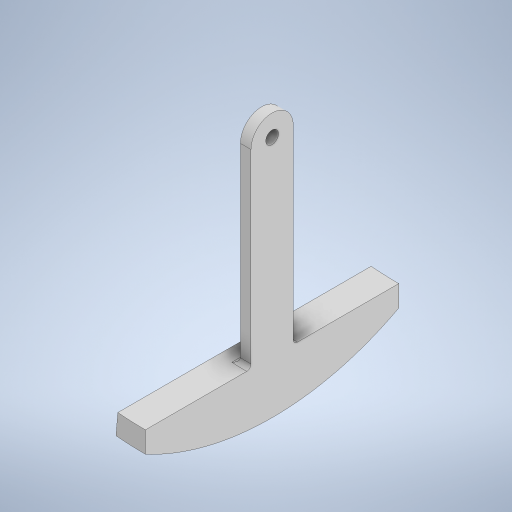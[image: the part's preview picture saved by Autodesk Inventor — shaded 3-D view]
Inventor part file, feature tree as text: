
AUTODESK INVENTOR PART (.ipt)
format: ipt  version: 2023 (Build 270158000, 158)  size: 271,360 bytes
history: native  units: mm
features: sketch x3, fillet x2, revolve x1, extrude x1, hole x1
ambient origin geometry x8: Origin, YZ Plane, XZ Plane, XY Plane, X Axis, Y Axis, Z Axis, Center Point
bodies: Body1 (feature_tree)
feature tree (8):
  revolve  "回転2"
  extrude  "押し出し1"  Depth=120.0mm
  fillet  "フィレット2"  Radius=10.0mm
  hole  "穴1"  [1 undecoded]
  fillet  "フィレット3"  Radius=25.0mm
  sketch  "スケッチ2"
  sketch  "スケッチ3"
  sketch  "スケッチ4"
note: 1 required parameter value undecoded (feature->parameter linkage not recoverable at this tier; creation-order binding heuristic only, values carry confidence <= 0.55)
